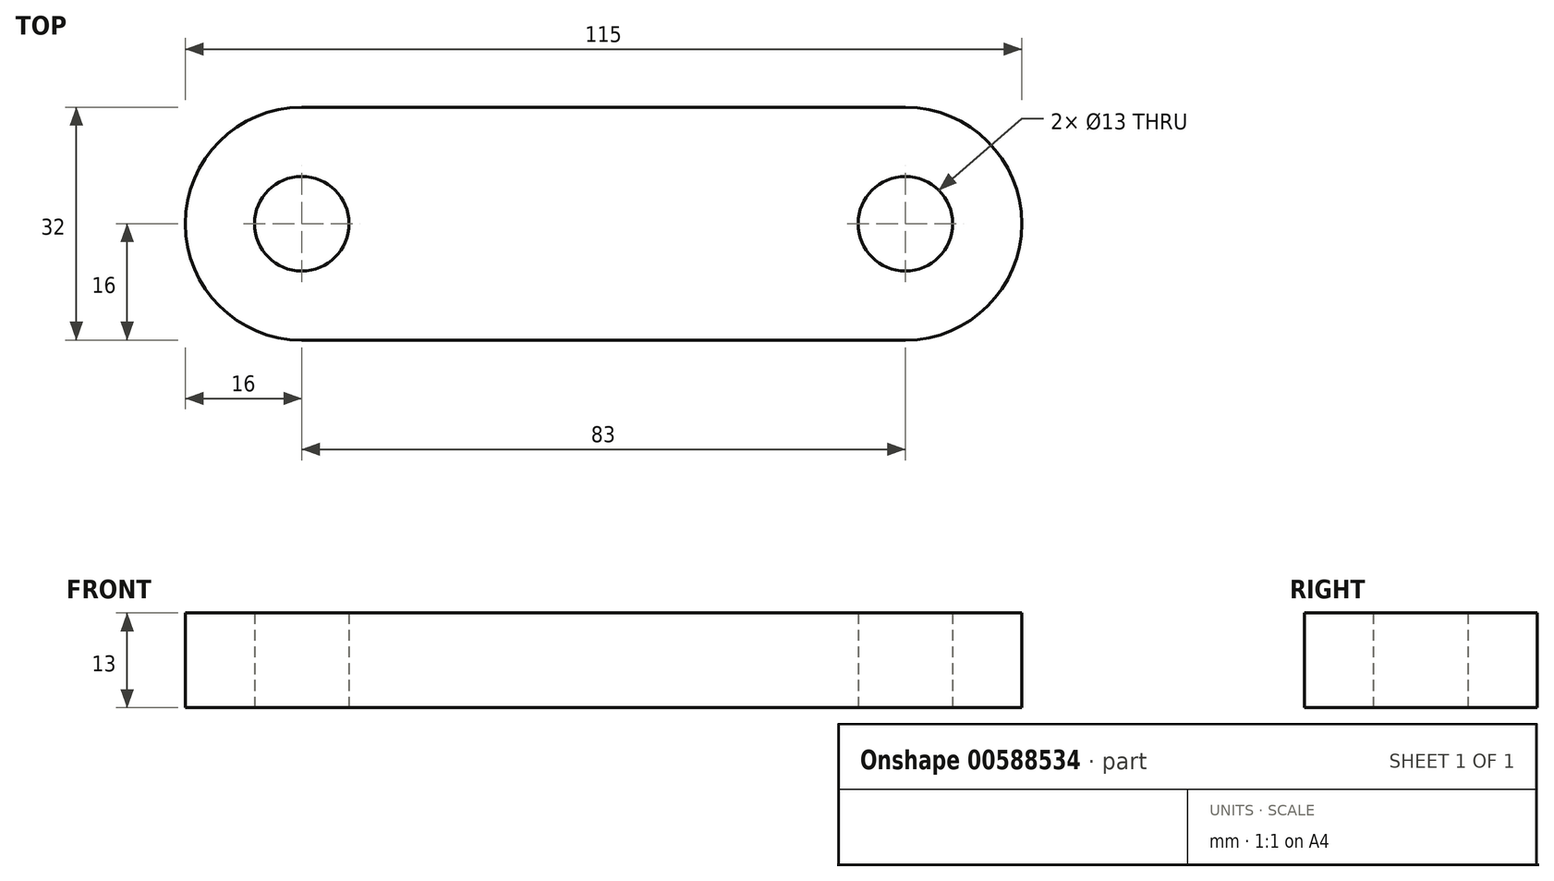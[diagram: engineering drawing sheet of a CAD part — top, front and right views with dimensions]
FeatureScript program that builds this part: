
annotation { "Feature Type Name" : "Feature", "Feature Type Description" : "" }
export const myFeature = defineFeature(function(context is Context, id is Id, definition is map)
    precondition{}
    {
        {
            var Q0;
            Q0=qCreatedBy(makeId("Top.planeOp"),FACE);
            var sketch = newSketch(context, id + "F0", { "sketchPlane" : qUnion([Q0])});
            skLineSegment(sketch, "E0.top", {"start": v(41.5, -32) * mm, "end": v(-41.5, -32) * mm});
            skArc(sketch, "E1", {"start": v(-41.5, 0) * mm, "mid": v(-57.5, -16) * mm, "end": v(-41.5, -32) * mm});
            skArc(sketch, "E2", {"start": v(41.5, -32) * mm, "mid": v(57.5, -16) * mm, "end": v(41.5, 0) * mm});
            skLineSegment(sketch, "E3", {"start": v(-41.5, 0) * mm, "end": v(41.5, 0) * mm});
            skCircle(sketch, "E4", {"center": v(41.5, -16) * mm, "radius": 6.5 * mm});
            skCircle(sketch, "E5", {"center": v(-41.5, -16) * mm, "radius": 6.5 * mm});
            skSolve(sketch);
        }
        {
            var Q0;
            Q0=makeQuery(id+"F0.imprint","IMPRINT",FACE,{"disambiguationData":[TD([[makeQuery(id+"F0.imprint","IMPRINT",EDGE,{"derivedFrom":sQuery(id+"F0.wireOp",EDGE,"E0.top")}),-1.0]])]});
            extrude(context, id + "F1", {"entities" : qUnion([Q0]), "depth" : 13 * mm, "offsetDistance" : 25 * mm});
        }
    });
